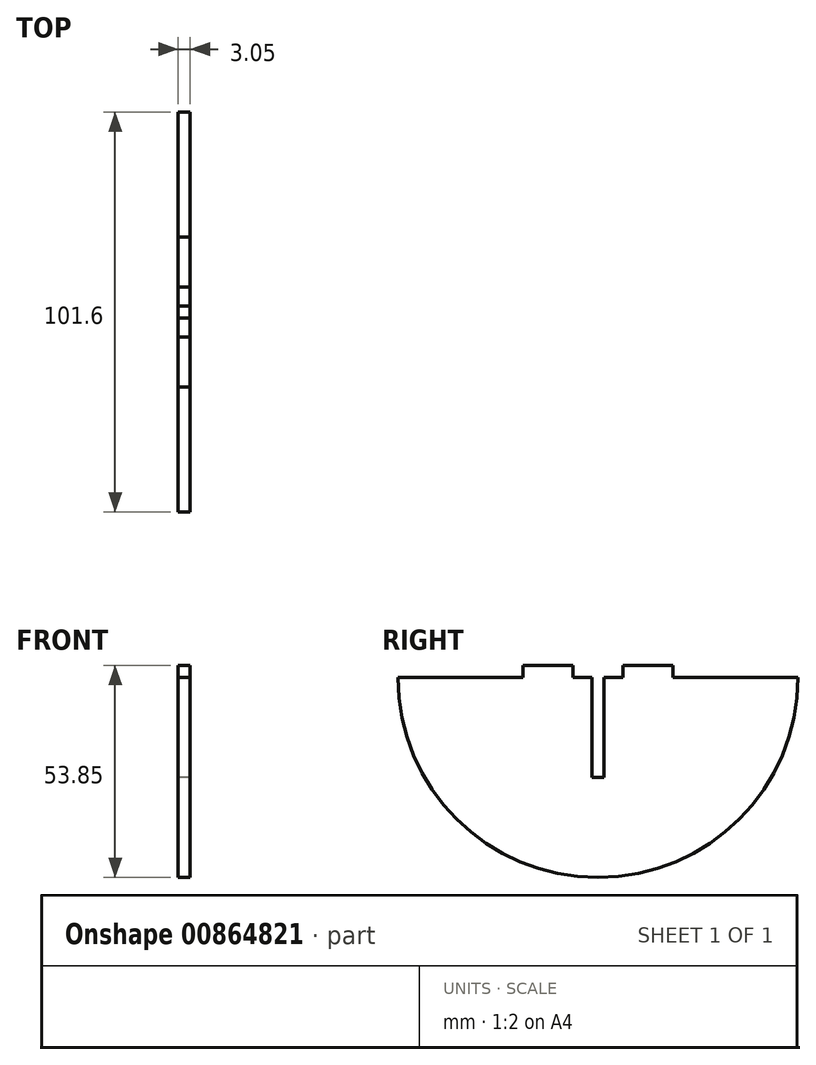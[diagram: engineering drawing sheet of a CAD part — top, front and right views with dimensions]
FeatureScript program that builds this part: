
annotation { "Feature Type Name" : "Feature", "Feature Type Description" : "" }
export const myFeature = defineFeature(function(context is Context, id is Id, definition is map)
    precondition{}
    {
        {
            var Q0;
            Q0=qCreatedBy(makeId("Right.planeOp"),FACE);
            var sketch = newSketch(context, id + "F0", { "sketchPlane" : qUnion([Q0])});
            skArc(sketch, "E0", {"start": v(-50.8, 50.8) * mm, "mid": v(0, 0) * mm, "end": v(50.8, 50.8) * mm});
            skLineSegment(sketch, "E1", {"start": v(-50.8, 50.8) * mm, "end": v(-1.52, 50.8) * mm, "construction": true});
            skLineSegment(sketch, "E2", {"start": v(-19.05, 53.85) * mm, "end": v(-6.35, 53.85) * mm});
            skLineSegment(sketch, "E3", {"start": v(-19.05, 53.85) * mm, "end": v(-19.05, 50.8) * mm});
            skLineSegment(sketch, "E4", {"start": v(-6.35, 53.85) * mm, "end": v(-6.35, 50.8) * mm});
            skLineSegment(sketch, "E5", {"start": v(6.35, 53.85) * mm, "end": v(6.35, 50.8) * mm});
            skLineSegment(sketch, "E6", {"start": v(19.05, 53.85) * mm, "end": v(19.05, 50.8) * mm});
            skLineSegment(sketch, "E7", {"start": v(-50.8, 50.8) * mm, "end": v(-19.05, 50.8) * mm});
            skLineSegment(sketch, "E8", {"start": v(19.05, 50.8) * mm, "end": v(50.8, 50.8) * mm});
            skLineSegment(sketch, "E9.trimOffspring", {"start": v(6.35, 53.85) * mm, "end": v(19.05, 53.85) * mm});
            skLineSegment(sketch, "E10", {"start": v(-6.35, 50.8) * mm, "end": v(-1.52, 50.8) * mm});
            skLineSegment(sketch, "E11", {"start": v(-1.52, 50.8) * mm, "end": v(-1.52, 25.4) * mm});
            skLineSegment(sketch, "E12", {"start": v(-1.52, 25.4) * mm, "end": v(1.52, 25.4) * mm});
            skLineSegment(sketch, "E13", {"start": v(1.52, 25.4) * mm, "end": v(1.52, 50.8) * mm});
            skLineSegment(sketch, "E14.trimOffspring", {"start": v(1.52, 50.8) * mm, "end": v(50.8, 50.8) * mm, "construction": true});
            skLineSegment(sketch, "E15.trimOffspring", {"start": v(1.52, 50.8) * mm, "end": v(6.35, 50.8) * mm});
            skSolve(sketch);
        }
        {
            var Q0;
            Q0 = qSketchRegion(id + "F0", true);
            extrude(context, id + "F1", {"entities" : qUnion([Q0]), "depth" : 3.05 * mm, "offsetDistance" : 25.4 * mm});
        }
    });
